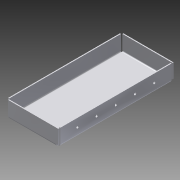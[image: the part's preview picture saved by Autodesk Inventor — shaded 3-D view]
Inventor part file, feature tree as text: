
AUTODESK INVENTOR PART (.ipt)
format: ipt  version: 2015 SP1 (Build 190203100, 203)  size: 231,424 bytes
history: native  units: in
note: dims shown in document units (in); Inventor stores cm internally (conversion verified against a paired STEP export)
features: sheet_metal_op x7, other x5, sketch x4, hole x1
ambient origin geometry x8: Origin, YZ Plane, XZ Plane, XY Plane, X Axis, Y Axis, Z Axis, Center Point
bodies: Solid1 (feature_tree)
feature tree (17):
  other  "<userpath>\Documents\2015 Offseason Chassis\West Coast Chassis Fall 2015\rivet(rv).xlsx"
  sheet_metal_op  "Face1"
  sheet_metal_op  "Flange1"
  sheet_metal_op  "Flange2"
  hole  "Hole2"  [1 undecoded]
  sketch  "Sketch1"  dims[d0=7.1in d1=3.2in]
  other  "Plate1"
  sketch  "Sketch3"  dims[d2=0.0625in]
  other  "Plate2"
  sheet_metal_op  "Bend1"
  sheet_metal_op  "Corner1"
  sketch  "Sketch4"  dims[d14=0.0625in]
  other  "Plate3"
  sheet_metal_op  "Bend2"
  sheet_metal_op  "Corner2"
  sketch  "Sketch5"  dims[d15=0.0312in d16=0.125in d17=0.0625in d18=1.0in d19=90.0deg d20=0.0625in d21=0.25in d22=0.0625in d23=0.0625in d24=0.0625in d25=0.0312in d26=0.125in d27=0.0625in d28=1.0in d29=90.0deg d30=0.0625in d31=0.25in d32=0.0625in d33=0.0625in d34=0.5in d35=0.1406in d36=0.339in d37=0.375in d38=0.25in d39=0.5635in d40=0.617in d41=0.8108in]
  other  "Definition1"
note: 1 required parameter value undecoded (feature->parameter linkage not recoverable at this tier; creation-order binding heuristic only, values carry confidence <= 0.55)
